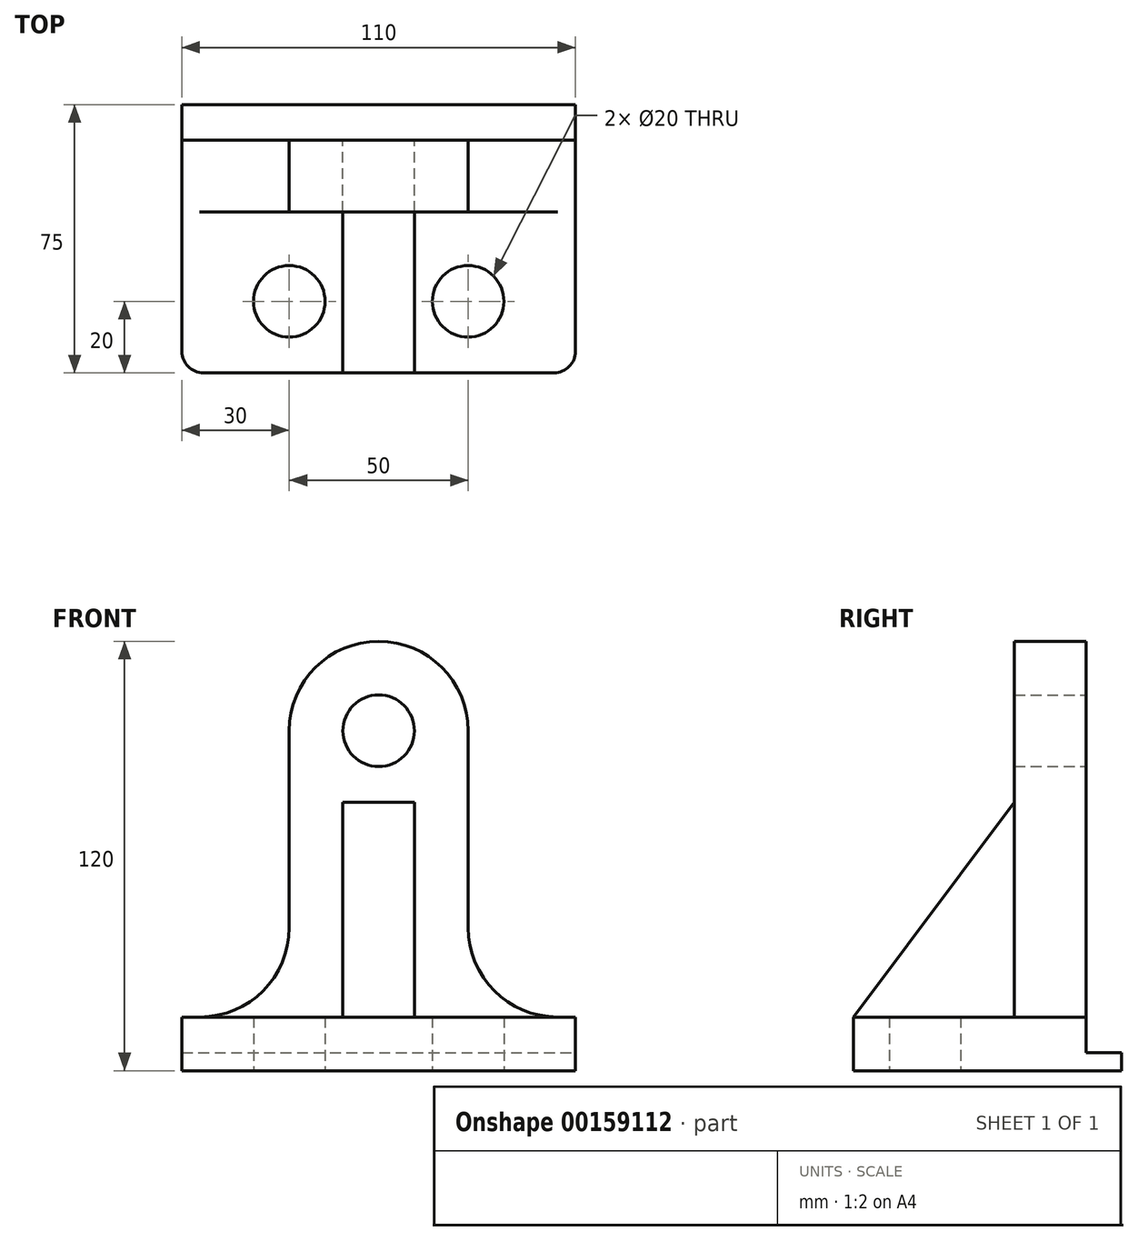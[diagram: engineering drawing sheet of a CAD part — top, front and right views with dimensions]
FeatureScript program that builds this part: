
annotation { "Feature Type Name" : "Feature", "Feature Type Description" : "" }
export const myFeature = defineFeature(function(context is Context, id is Id, definition is map)
    precondition{}
    {
        {
            var Q0;
            Q0=qCreatedBy(makeId("Top.planeOp"),FACE);
            var sketch = newSketch(context, id + "F0", { "sketchPlane" : qUnion([Q0])});
            skLineSegment(sketch, "E0.bottom", {"start": v(-55, 75) * mm, "end": v(55, 75) * mm});
            skLineSegment(sketch, "E0.top", {"start": v(-49, 0) * mm, "end": v(49, 0) * mm});
            skLineSegment(sketch, "E0.left", {"start": v(-55, 75) * mm, "end": v(-55, 6) * mm});
            skLineSegment(sketch, "E0.right", {"start": v(55, 75) * mm, "end": v(55, 6) * mm});
            skPoint(sketch, "E1.visualSharp", {"position": v(55, 0) * mm});
            skArc(sketch, "E1.filletArc", {"start": v(49, 0) * mm, "mid": v(53.24, 1.76) * mm, "end": v(55, 6) * mm});
            skPoint(sketch, "E2.visualSharp", {"position": v(-55, 0) * mm});
            skArc(sketch, "E2.filletArc", {"start": v(-55, 6) * mm, "mid": v(-53.24, 1.76) * mm, "end": v(-49, 0) * mm});
            skCircle(sketch, "E3", {"center": v(25, 20) * mm, "radius": 10 * mm});
            skCircle(sketch, "E4", {"center": v(-25, 20) * mm, "radius": 10 * mm});
            skLineSegment(sketch, "E5", {"start": v(0, 20) * mm, "end": v(0, 0) * mm, "construction": true});
            skLineSegment(sketch, "E6", {"start": v(-25, 20) * mm, "end": v(25, 20) * mm});
            skSolve(sketch);
        }
        {
            var Q0;
            Q0 = qSketchRegion(id + "F0", true);
            extrude(context, id + "F1", {"entities" : qUnion([Q0]), "depth" : 15 * mm});
        }
        {
            var Q0;
            Q0=makeQuery(id+"F1.opExtrude","SWEPT_FACE",FACE,{"disambiguationData":[OSD([sQuery(id+"F0.wireOp",EDGE,"E0.bottom")])]});
            var sketch = newSketch(context, id + "F2", { "sketchPlane" : qUnion([Q0])});
            skLineSegment(sketch, "E7", {"start": v(25, 40) * mm, "end": v(25, 95) * mm});
            skLineSegment(sketch, "E8", {"start": v(-25, 40) * mm, "end": v(-25, 95) * mm});
            skArc(sketch, "E9", {"start": v(25, 95) * mm, "mid": v(0, 120) * mm, "end": v(-25, 95) * mm});
            skArc(sketch, "E10", {"start": v(-50, 15) * mm, "mid": v(-32.32, 22.32) * mm, "end": v(-25, 40) * mm});
            skArc(sketch, "E11", {"start": v(25, 40) * mm, "mid": v(32.32, 22.32) * mm, "end": v(50, 15) * mm});
            skCircle(sketch, "E12", {"center": v(0, 95) * mm, "radius": 10 * mm});
            skLineSegment(sketch, "E13", {"start": v(50, 15) * mm, "end": v(-50, 15) * mm});
            skSolve(sketch);
        }
        {
            var Q0;
            Q0=makeQuery(id+"F2.imprint","IMPRINT",FACE,{"disambiguationData":[TD([[makeQuery(id+"F2.imprint","IMPRINT",EDGE,{"derivedFrom":sQuery(id+"F2.wireOp",EDGE,"E7")}),1.0]])]});
            extrude(context, id + "F3", {"entities" : qUnion([Q0]), "operationType" : NewBodyOperationType.ADD, "oppositeDirection" : true, "depth" : 30 * mm, "hasSecondDirection" : true, "secondDirectionOppositeDirection" : true, "secondDirectionDepth" : 10 * mm});
        }
        {
            var Q0;
            Q0=qCreatedBy(makeId("Right.planeOp"),FACE);
            var sketch = newSketch(context, id + "F4", { "sketchPlane" : qUnion([Q0])});
            skLineSegment(sketch, "E14", {"start": v(0, 15) * mm, "end": v(45, 15) * mm});
            skLineSegment(sketch, "E15", {"start": v(45, 15) * mm, "end": v(45, 75) * mm});
            skLineSegment(sketch, "E16", {"start": v(45, 75) * mm, "end": v(0, 15) * mm});
            skSolve(sketch);
        }
        {
            var Q0;
            Q0 = qSketchRegion(id + "F4", true);
            extrude(context, id + "F5", {"entities" : qUnion([Q0]), "operationType" : NewBodyOperationType.ADD, "depth" : 10 * mm, "hasSecondDirection" : true, "secondDirectionOppositeDirection" : true, "secondDirectionDepth" : 10 * mm});
        }
        {
            var Q0;
            Q0=makeQuery(id+"F1.opExtrude","SWEPT_FACE",FACE,{"disambiguationData":[OSD([sQuery(id+"F0.wireOp",EDGE,"E0.right")])]});
            var sketch = newSketch(context, id + "F6", { "sketchPlane" : qUnion([Q0])});
            skLineSegment(sketch, "E17.bottom", {"start": v(65, 15) * mm, "end": v(75, 15) * mm});
            skLineSegment(sketch, "E17.left", {"start": v(65, 15) * mm, "end": v(65, 5) * mm});
            skLineSegment(sketch, "E18", {"start": v(75, 15) * mm, "end": v(75, 5) * mm});
            skLineSegment(sketch, "E19", {"start": v(75, 5) * mm, "end": v(65, 5) * mm});
            skSolve(sketch);
        }
        {
            var Q0;
            Q0 = qSketchRegion(id + "F6", true);
            extrude(context, id + "F7", {"entities" : qUnion([Q0]), "operationType" : NewBodyOperationType.REMOVE, "endBound" : BoundingType.THROUGH_ALL, "oppositeDirection" : true, "depth" : 25 * mm});
        }
    });
